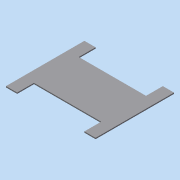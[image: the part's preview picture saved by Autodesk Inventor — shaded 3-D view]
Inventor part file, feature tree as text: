
AUTODESK INVENTOR PART (.ipt)
format: ipt  version: 2014 SP2 (Build 180246200, 246)  size: 81,920 bytes
history: native  units: mm
features: extrude x1, sketch x1
ambient origin geometry x8: Origin, YZ Plane, XZ Plane, XY Plane, X Axis, Y Axis, Z Axis, Center Point
bodies: Volumenkörper1 (feature_tree)
feature tree (2):
  extrude  "Extrusion1"  Depth=200.0mm
  sketch  "Skizze1"  dims[d0=400.0mm d1=200.0mm d2=50.0mm d3=75.0mm d4=5.0mm d5=0.0mm]
